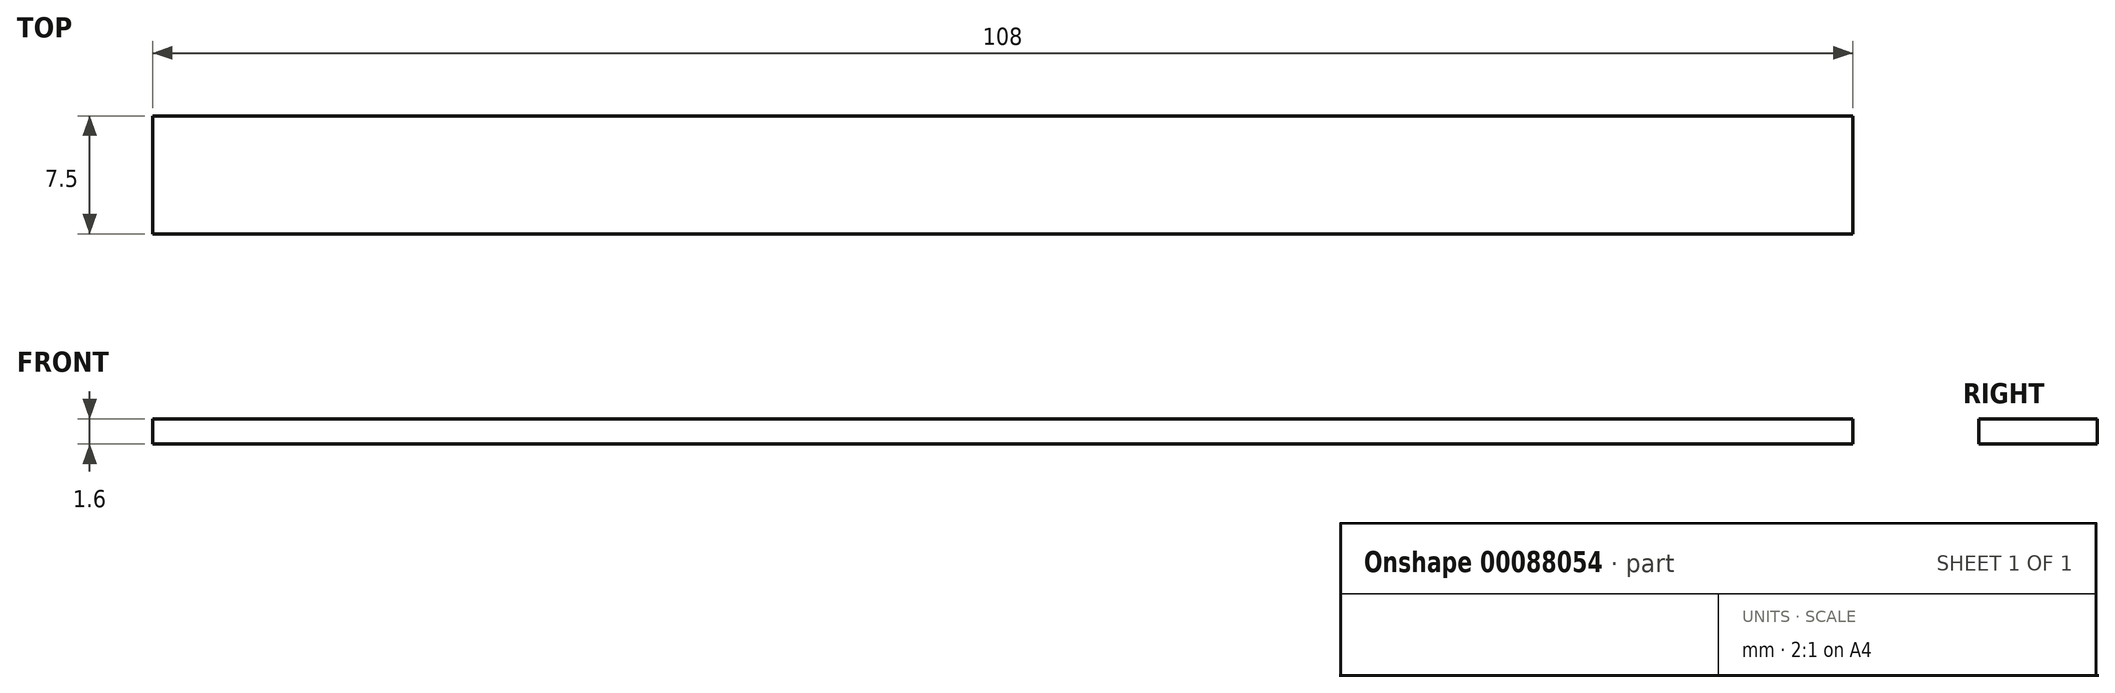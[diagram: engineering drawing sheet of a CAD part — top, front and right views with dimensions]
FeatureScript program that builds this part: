
annotation { "Feature Type Name" : "Feature", "Feature Type Description" : "" }
export const myFeature = defineFeature(function(context is Context, id is Id, definition is map)
    precondition{}
    {
        {
            var Q0;
            Q0=qCreatedBy(makeId("Top.planeOp"),FACE);
            var sketch = newSketch(context, id + "F0", { "sketchPlane" : qUnion([Q0])});
            skLineSegment(sketch, "E0.bottom", {"start": v(-54, 3.75) * mm, "end": v(54, 3.75) * mm});
            skLineSegment(sketch, "E0.top", {"start": v(-54, -3.75) * mm, "end": v(54, -3.75) * mm});
            skLineSegment(sketch, "E0.left", {"start": v(-54, 3.75) * mm, "end": v(-54, -3.75) * mm});
            skLineSegment(sketch, "E0.right", {"start": v(54, 3.75) * mm, "end": v(54, -3.75) * mm});
            skPoint(sketch, "E0.middle", {"position": v(0, 0) * mm});
            skSolve(sketch);
        }
        {
            var Q0;
            Q0 = qSketchRegion(id + "F0", true);
            extrude(context, id + "F1", {"entities" : qUnion([Q0]), "depth" : 1.6 * mm, "offsetDistance" : 25 * mm});
        }
    });
